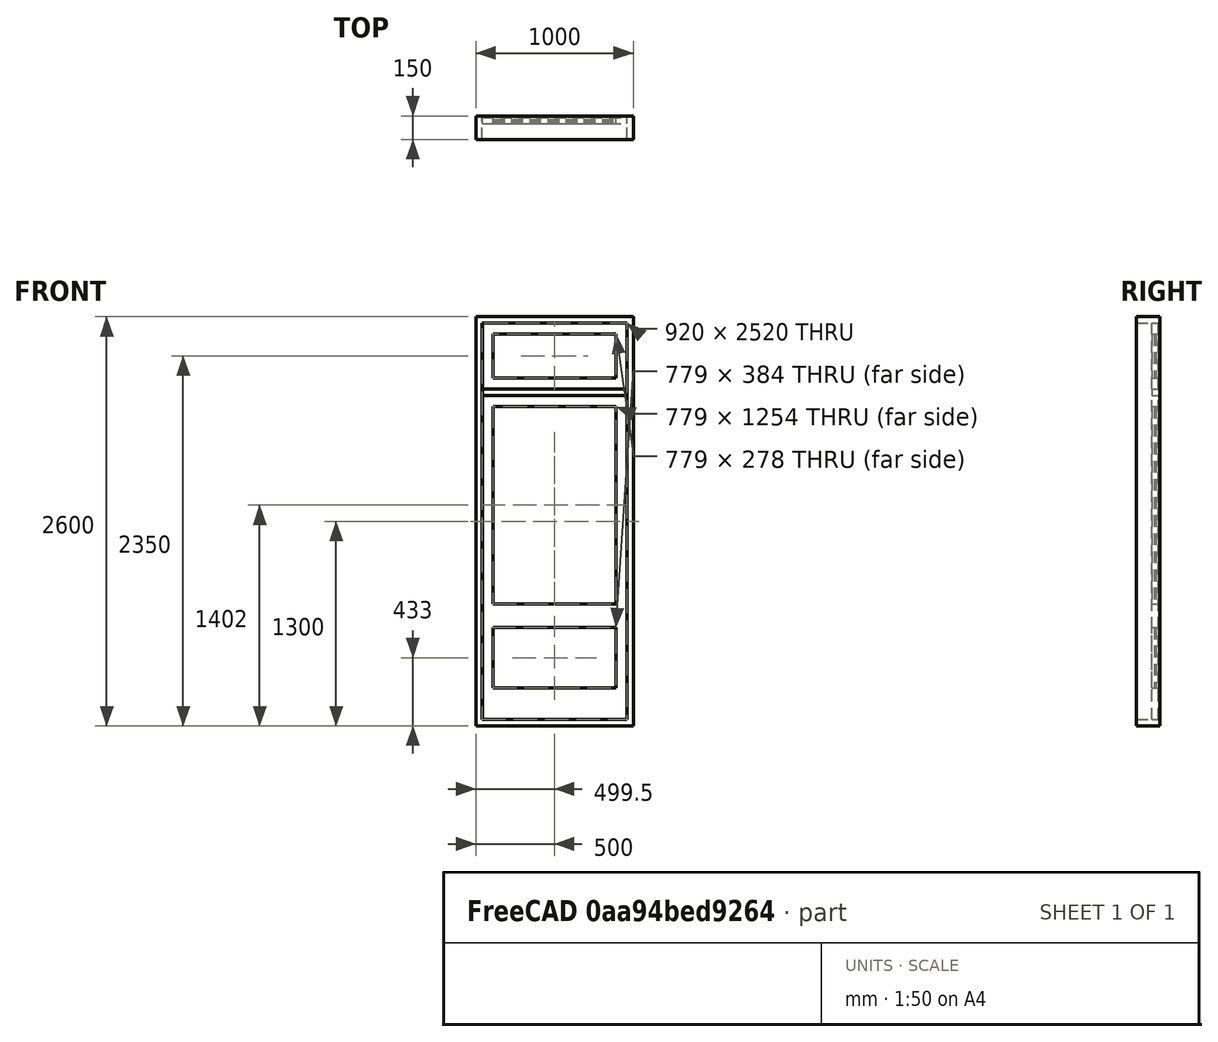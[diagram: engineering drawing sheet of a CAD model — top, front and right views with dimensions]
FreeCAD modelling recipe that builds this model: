
FCSTD DOCUMENT  (FreeCAD 0.16R6704 (Git))
Label: Single elevated door with glass and transom
License: CreativeCommons Attribution
LicenseURL: http://creativecommons.org/licenses/by/4.0/
objects: Sketcher::SketchObject×1, Part::FeaturePython×1
note: 2 computed .brp shape members not serialized (recipe doc carries the construction recipe); baked Part::Feature solids carry a one-line shape summary decoded from their .brp

FEATURE [Sketcher::SketchObject] Sketch178  label="Sketch"
  Placement = pos=(0,0,0) rot=(1,0,0;1.5708rad)
  sketch-geometry (33):
    g0: LineSegment StartX=0 StartY=360 StartZ=0 EndX=1000 EndY=360 EndZ=0
    g1: LineSegment StartX=1000 StartY=360 StartZ=0 EndX=1000 EndY=2960 EndZ=0
    g2: LineSegment StartX=1000 StartY=2960 StartZ=0 EndX=0 EndY=2960 EndZ=0
    g3: LineSegment StartX=0 StartY=2960 StartZ=0 EndX=0 EndY=360 EndZ=0
    g4: LineSegment StartX=40 StartY=400 StartZ=0 EndX=960 EndY=400 EndZ=0
    g5: LineSegment StartX=960 StartY=400 StartZ=0 EndX=960 EndY=2920 EndZ=0
    g6: LineSegment StartX=960 StartY=2920 StartZ=0 EndX=40 EndY=2920 EndZ=0
    g7: LineSegment StartX=40 StartY=2920 StartZ=0 EndX=40 EndY=400 EndZ=0
    g8: LineSegment StartX=110 StartY=2389 StartZ=0 EndX=889 EndY=2389 EndZ=0
    g9: LineSegment StartX=889 StartY=2389 StartZ=0 EndX=889 EndY=1135 EndZ=0
    g10: LineSegment StartX=889 StartY=1135 StartZ=0 EndX=110 EndY=1135 EndZ=0
    g11: LineSegment StartX=110 StartY=1135 StartZ=0 EndX=110 EndY=2389 EndZ=0
    g12: LineSegment StartX=110 StartY=985 StartZ=0 EndX=889 EndY=985 EndZ=0
    g13: LineSegment StartX=889 StartY=985 StartZ=0 EndX=889 EndY=601 EndZ=0
    g14: LineSegment StartX=889 StartY=601 StartZ=0 EndX=110 EndY=601 EndZ=0
    g15: LineSegment StartX=110 StartY=601 StartZ=0 EndX=110 EndY=985 EndZ=0
    g16: LineSegment [constr] StartX=-278 StartY=1060 StartZ=0 EndX=1352 EndY=1060 EndZ=0
    g17: LineSegment StartX=41 StartY=2459 StartZ=0 EndX=959 EndY=2459 EndZ=0
    g18: LineSegment StartX=959 StartY=2459 StartZ=0 EndX=959 EndY=401 EndZ=0
    g19: LineSegment StartX=959 StartY=401 StartZ=0 EndX=41 EndY=401 EndZ=0
    g20: LineSegment StartX=41 StartY=401 StartZ=0 EndX=41 EndY=2459 EndZ=0
    g21: LineSegment StartX=41 StartY=2919 StartZ=0 EndX=959 EndY=2919 EndZ=0
    g22: LineSegment StartX=959 StartY=2919 StartZ=0 EndX=959 EndY=2501 EndZ=0
    g23: LineSegment StartX=959 StartY=2501 StartZ=0 EndX=41 EndY=2501 EndZ=0
    g24: LineSegment StartX=41 StartY=2501 StartZ=0 EndX=41 EndY=2919 EndZ=0
    g25: LineSegment StartX=110 StartY=2849 StartZ=0 EndX=889 EndY=2849 EndZ=0
    g26: LineSegment StartX=889 StartY=2849 StartZ=0 EndX=889 EndY=2571 EndZ=0
    g27: LineSegment StartX=889 StartY=2571 StartZ=0 EndX=110 EndY=2571 EndZ=0
    g28: LineSegment StartX=110 StartY=2571 StartZ=0 EndX=110 EndY=2849 EndZ=0
    g29: LineSegment StartX=41 StartY=2500 StartZ=0 EndX=959 EndY=2500 EndZ=0
    g30: LineSegment StartX=959 StartY=2500 StartZ=0 EndX=959 EndY=2460 EndZ=0
    g31: LineSegment StartX=959 StartY=2460 StartZ=0 EndX=41 EndY=2460 EndZ=0
    g32: LineSegment StartX=41 StartY=2460 StartZ=0 EndX=41 EndY=2500 EndZ=0
  constraints (98):
    c: Coincident(g0,g1)
    c: Coincident(g1,g2)
    c: Coincident(g2,g3)
    c: Coincident(g3,g0)
    c: Horizontal(g0)
    c: Horizontal(g2)
    c: Vertical(g1)
    c: Vertical(g3)
    c: Coincident(g4,g5)
    c: Coincident(g5,g6)
    c: Coincident(g6,g7)
    c: Coincident(g7,g4)
    c: Horizontal(g4)
    c: Horizontal(g6)
    c: Vertical(g5)
    c: Vertical(g7)
    c: DistanceX(g0) = 1000  'Largura do vão'
    c: DistanceY(g6,g2) = 40  'batente 2'
    c: DistanceX(g2,g6) = 40  'Batente 1'
    c: DistanceX(g4,g0) = 40  'Batente 3'
    c: Coincident(g8,g9)
    c: Coincident(g9,g10)
    c: Coincident(g10,g11)
    c: Coincident(g11,g8)
    c: Horizontal(g8)
    c: Horizontal(g10)
    c: Vertical(g9)
    c: Vertical(g11)
    c: Coincident(g12,g13)
    c: Coincident(g13,g14)
    c: Coincident(g14,g15)
    c: Coincident(g15,g12)
    c: Horizontal(g12)
    c: Horizontal(g14)
    c: Vertical(g13)
    c: Vertical(g15)
    c: DistanceX(g10,g12) = 0
    c: DistanceX(g9,g12) = 0
    c: DistanceY(g12,g10) = 150  'Moldura intermediária porta'
    c: DistanceX(g6,g8) = 70  'Moldura vertical 1 porta'
    c: Horizontal(g16)  'Constraint45'
    c: Symmetric(g10,g12,g16)  'Constraint44'
    c: Coincident(g17,g18)
    c: Coincident(g18,g19)
    c: Coincident(g19,g20)
    c: Coincident(g20,g17)
    c: Horizontal(g17)
    c: Horizontal(g19)
    c: Vertical(g18)
    c: Vertical(g20)
    c: DistanceX(g18,g4) = 1
    c: DistanceX(g6,g17) = 1
    c: DistanceY(g8,g17) = 70  'Altura da moldura superior porta'
    c: Coincident(g21,g22)  'Constraint59'
    c: Coincident(g22,g23)  'Constraint57'
    c: Coincident(g23,g24)
    c: Coincident(g24,g21)
    c: Horizontal(g21)
    c: Horizontal(g23)
    c: Vertical(g22)
    c: Vertical(g24)
    c: Coincident(g25,g26)
    c: Coincident(g26,g27)
    c: Coincident(g27,g28)
    c: Coincident(g28,g25)
    c: Horizontal(g25)
    c: Horizontal(g27)
    c: Vertical(g26)
    c: Vertical(g28)
    c: DistanceY(g25,g21) = 70  'Altura moldura bandeira'
    c: DistanceY(g22,g26) = 70  'Altura da moldura bandeira 2'
    c: DistanceX(g8,g26) = 0  'Constraint80'
    c: DistanceY(g21,g6) = 1  'Constraint77'
    c: DistanceX(g8,g27) = 0  'Constraint75'
    c: Coincident(g29,g30)  'Constraint84'
    c: Coincident(g30,g31)  'Constraint76'
    c: Coincident(g31,g32)
    c: Horizontal(g29)
    c: Horizontal(g31)
    c: Vertical(g30)
    c: Vertical(g32)
    c: DistanceY(g17,g31) = 1
    c: DistanceX(g23,g29) = 0
    c: DistanceY(g29,g23) = 1
    c: DistanceX(g30,g17) = 0
    c: DistanceX(g22,g29) = 0
    c: DistanceX(g25,g21) = 70  'Largura moldura 2'
    c: DistanceX(g17,g31) = 0
    c: Coincident(g32,g29)
    c: DistanceY(g31,g29) = 40  'Batente bandeira'
    c: DistanceY(g19,g14) = 200  'Altura da moldura inferior porta'
    c: DistanceY(g4,g19) = 1  'Constraint96'
    c: DistanceY(g0,g4) = 40  'Altura perfil peitoril'
    c: DistanceX(g-1,g0) = 0
    c: DistanceY(g-1,g4) = 400  'Altura peitoril'
    c: DistanceY(g0,g16) = 700  'Altura do montante intermediário'
    c: DistanceY(g4,g29) = 2100  'Altura até a bandeira'
    c: DistanceY(g0,g1) = 2600  'Altura da abertura'
FEATURE [Part::FeaturePython] Window111  label="Single elevated door with glass and transom "  # WARN: FeaturePython — macro-defined, semantics opaque (R4)
  Base = -> Sketch178
  Height = 2100
  HoleDepth = 0
  MoveWithHost = true
  Normal = (0,1,0)
  Preset = 6
  Role = 1
  Width = 900
  WindowParts = BATENTE | Frame | Wire0,Wire1 | 150.0 | 0.0 | PORTA | Frame | Wire2,Wire3,Wire4 | 40.0 | 100.0 | BANDEIRA | Frame | Wire6,Wire5 | 40.0 | 100.0 | BATENTE BANDEIRA | Frame | Wire7 | 50.0 | 100.0 | VIDRO BANDEIRA | Glass panel | Wire6 | 10.0 | 115.0 | VIDRO SUPERIOR PORTA | Glass panel | Wire2 | 10.0 | 115.0 | VIDRO INFERIOR PORTA | Glass panel | Wire3 | 10.0 | 115.0
